# Revit family: Vitreous china wall-hung bidet - Meridian - Roca - 357245..0
name_source: partatom
category: Plumbing Fixtures
revit_build: Autodesk Revit Architecture 2014 (Build: 20130308_1515(x64)
units: mm (PartAtom-declared; Revit-internal decimal feet)

## types (2) — shared parameters
BIMobject category = Bidets
Depth = 360.00
Description = Vitreous china wall-hung bidet
Design country = Spain
Eco green certification = No
Edition number = 1
Height = 300 mm
IFC Classification = Furniture
Installation type = Wall-hung
Length = 360 mm  [stored 1.1811 ft]
Manufacturer name = Roca
Manufacturer url = http://www.roca.com
Model = 357245..0
NBS Reference Code = 35-06-11
NBS Reference Description = Bidets
Nominal height = 300.00
Nominal width = 560.00
Outlet Diameter = 46 mm  [stored 0.150919 ft]
Product data url = http://roca.bimobject.com
Product family = Meridian
Product group = Bidet
QR code = http://roca.bimobject.com
Shape = Round
Suitable for Children = No
Suitable for Handicapped = No
Taphole configuration = 1 Taphole
Taphole configuration: 1 Taphole
Tapholes Diameter = 35 mm  [stored 0.114829 ft]
Technical description = http://www.roca.com
UNSPSC Code = 301815
UNSPSC Name = Sanitary ware
URL = http://www.roca.com
Uniclass 1.4 Code = L7215
Uniclass 1.4 Description = Bidets
Uniclass 2.0 Code = PR-35-06-11
Uniclass 2.0 Description = Bidets
Weight Net (Kg) = 0
Width = 560 mm  [stored 1.83727 ft]

## per-type parameters (varying)
| type | Product SKU |
| White - Meridian - Roca | A357245000 |
| Pergamon - Meridian - Roca | A357245170 |

note: column(s) folded — value = type name in every type: Material

note: [stored X ft] marks values corroborated as IEEE doubles in the binary element streams (Revit-internal decimal feet)

## geometry (parser evidence)
native form markers: Sweep x2
no freeform markers — native parametric forms only
